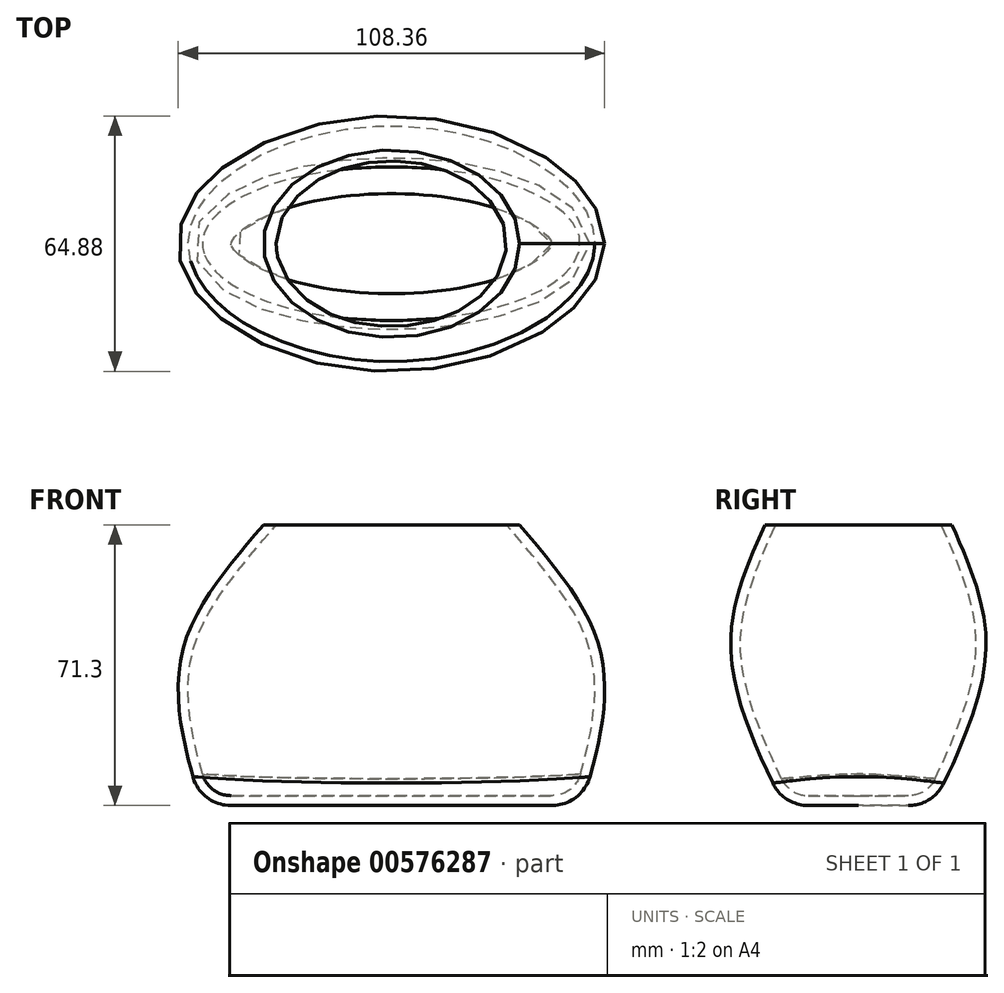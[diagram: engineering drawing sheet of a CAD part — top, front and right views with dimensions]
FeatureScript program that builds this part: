
annotation { "Feature Type Name" : "Feature", "Feature Type Description" : "" }
export const myFeature = defineFeature(function(context is Context, id is Id, definition is map)
    precondition{}
    {
        {
            var Q0;
            Q0=qCreatedBy(makeId("Top.planeOp"),FACE);
            var sketch = newSketch(context, id + "F0", { "sketchPlane" : qUnion([Q0])});
            skEllipse(sketch, "E0", {"center": v(0, 0) * mm, "majorRadius": 48.3 * mm, "minorRadius": 19.02 * mm, "majorAxis": v(1, 0)});
            skSolve(sketch);
        }
        {
            var Q0;
            Q0=qCreatedBy(makeId("Top.planeOp"),FACE);
            cPlane(context, id + "F1", {"entities" : qUnion([Q0]), "cplaneType" : CPlaneType.OFFSET, "offset" : 43.2 * mm, "width" : 150 * mm, "height" : 150 * mm});
        }
        {
            var Q0;
            Q0=qCreatedBy(id+"F1.planeOp",FACE);
            var sketch = newSketch(context, id + "F2", { "sketchPlane" : qUnion([Q0])});
            skEllipse(sketch, "E1", {"center": v(0, 0) * mm, "majorRadius": 51.86 * mm, "minorRadius": 32.4 * mm, "majorAxis": v(1, 0)});
            skSolve(sketch);
        }
        {
            var Q0;
            Q0=qCreatedBy(makeId("Top.planeOp"),FACE);
            cPlane(context, id + "F3", {"entities" : qUnion([Q0]), "cplaneType" : CPlaneType.OFFSET, "offset" : 71.3 * mm, "width" : 150 * mm, "height" : 150 * mm});
        }
        {
            var Q0;
            Q0=qCreatedBy(id+"F3.planeOp",FACE);
            var sketch = newSketch(context, id + "F4", { "sketchPlane" : qUnion([Q0])});
            skEllipse(sketch, "E2", {"center": v(0, 0) * mm, "majorRadius": 32.54 * mm, "minorRadius": 23.79 * mm, "majorAxis": v(1, 0)});
            skSolve(sketch);
        }
        {
            var Q0;
            Q0=makeQuery(id+"F0.imprint","IMPRINT",FACE,{"disambiguationData":[TD([[makeQuery(id+"F0.imprint","IMPRINT",EDGE,{"derivedFrom":sQuery(id+"F0.wireOp",EDGE,"E0")}),1.0]])]});
            var Q1;
            Q1=makeQuery(id+"F2.imprint","IMPRINT",FACE,{"disambiguationData":[TD([[makeQuery(id+"F2.imprint","IMPRINT",EDGE,{"derivedFrom":sQuery(id+"F2.wireOp",EDGE,"E1")}),1.0]])]});
            var Q2;
            Q2=makeQuery(id+"F4.imprint","IMPRINT",FACE,{"disambiguationData":[TD([[makeQuery(id+"F4.imprint","IMPRINT",EDGE,{"derivedFrom":sQuery(id+"F4.wireOp",EDGE,"E2")}),1.0]])]});
            loft(context, id + "F5", {"sheetProfilesArray" : [{ "sheetProfileEntities" : qUnion([Q0]) }, { "sheetProfileEntities" : qUnion([Q1]) }, { "sheetProfileEntities" : qUnion([Q2]) }]});
        }
        {
            var Q0;
            Q0=makeQuery(id+"F5.opLoft","CAP_FACE",FACE,{"disambiguationData":[OSD([makeQuery(id+"F0.imprint","IMPRINT",FACE,{"disambiguationData":[TD([[makeQuery(id+"F0.imprint","IMPRINT",EDGE,{"derivedFrom":sQuery(id+"F0.wireOp",EDGE,"E0")}),1.0]])]})])],"isStart":true});
            fillet(context, id + "F6", {"entities" : qUnion([Q0]), "radius" : 10 * mm, "tangentPropagation" : true, "allowEdgeOverflow" : false});
        }
        {
            var Q0;
            Q0=makeQuery(id+"F5.opLoft","CAP_FACE",FACE,{"disambiguationData":[OSD([makeQuery(id+"F4.imprint","IMPRINT",FACE,{"disambiguationData":[TD([[makeQuery(id+"F4.imprint","IMPRINT",EDGE,{"derivedFrom":sQuery(id+"F4.wireOp",EDGE,"E2")}),1.0]])]})])],"isStart":true});
            shell(context, id + "F7", {"entities" : qUnion([Q0]), "thickness" : 2.5 * mm});
        }
    });
